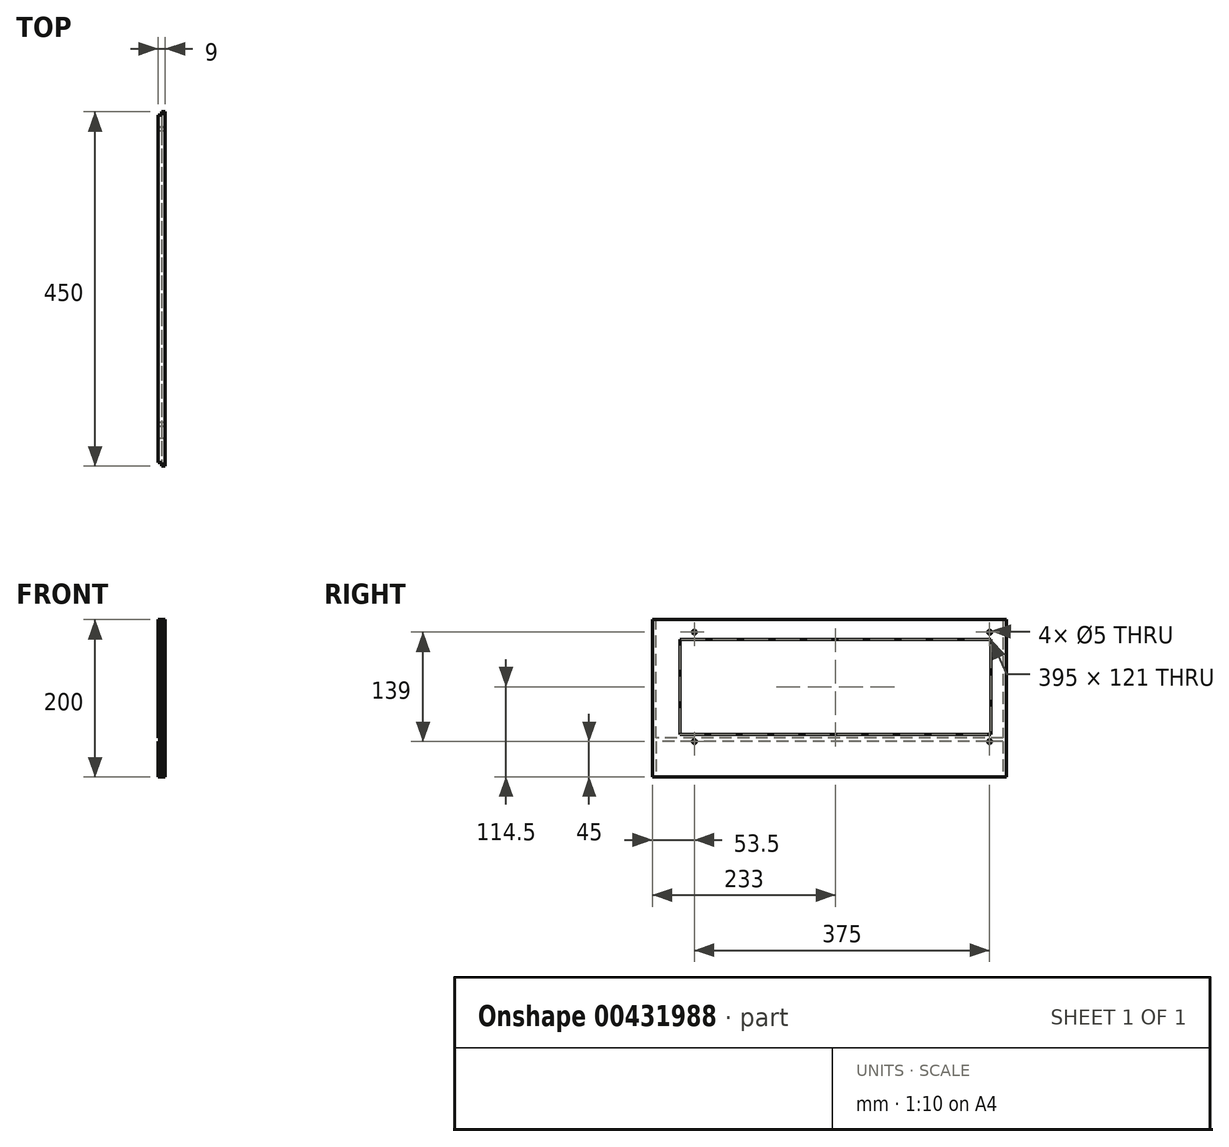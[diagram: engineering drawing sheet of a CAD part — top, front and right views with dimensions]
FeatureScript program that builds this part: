
annotation { "Feature Type Name" : "Feature", "Feature Type Description" : "" }
export const myFeature = defineFeature(function(context is Context, id is Id, definition is map)
    precondition{}
    {
        {
            var Q0;
            Q0=qCreatedBy(makeId("Right.planeOp"),FACE);
            var sketch = newSketch(context, id + "F0", { "sketchPlane" : qUnion([Q0])});
            skLineSegment(sketch, "E0.bottom", {"start": v(-225, 100) * mm, "end": v(225, 100) * mm});
            skLineSegment(sketch, "E0.top", {"start": v(-225, -100) * mm, "end": v(225, -100) * mm});
            skLineSegment(sketch, "E0.left", {"start": v(-225, 100) * mm, "end": v(-225, -100) * mm});
            skLineSegment(sketch, "E0.right", {"start": v(225, 100) * mm, "end": v(225, -100) * mm});
            skPoint(sketch, "E0.middle", {"position": v(0, 0) * mm});
            skSolve(sketch);
        }
        {
            var Q0;
            Q0=makeQuery(id+"F0.imprint","IMPRINT",FACE,{"disambiguationData":[TD([[makeQuery(id+"F0.imprint","IMPRINT",EDGE,{"derivedFrom":sQuery(id+"F0.wireOp",EDGE,"E0.bottom")}),-1.0]])]});
            extrude(context, id + "F1", {"entities" : qUnion([Q0]), "depth" : 9 * mm, "offsetDistance" : 25 * mm});
        }
        {
            var Q0;
            Q0=makeQuery(id+"F1.opExtrude","SWEPT_FACE",FACE,{"disambiguationData":[OSD([sQuery(id+"F0.wireOp",EDGE,"E0.left")])]});
            var sketch = newSketch(context, id + "F2", { "sketchPlane" : qUnion([Q0])});
            skLineSegment(sketch, "E1.bottom", {"start": v(0, -100) * mm, "end": v(4.5, -100) * mm});
            skLineSegment(sketch, "E1.top", {"start": v(0, 100) * mm, "end": v(4.5, 100) * mm});
            skLineSegment(sketch, "E1.left", {"start": v(0, -100) * mm, "end": v(0, 100) * mm});
            skLineSegment(sketch, "E1.right", {"start": v(4.5, -100) * mm, "end": v(4.5, 100) * mm});
            skSolve(sketch);
        }
        {
            var Q0;
            Q0=qSketchRegion(id+"F2",true);
            extrude(context, id + "F3", {"entities" : qUnion([Q0]), "operationType" : NewBodyOperationType.REMOVE, "oppositeDirection" : true, "depth" : 4.5 * mm, "offsetDistance" : 25 * mm});
        }
        {
            var Q0;
            Q0=makeQuery(id+"F1.opExtrude","SWEPT_FACE",FACE,{"disambiguationData":[OSD([sQuery(id+"F0.wireOp",EDGE,"E0.right")])]});
            var sketch = newSketch(context, id + "F4", { "sketchPlane" : qUnion([Q0])});
            skLineSegment(sketch, "E2.bottom", {"start": v(0, 100) * mm, "end": v(-4.5, 100) * mm});
            skLineSegment(sketch, "E2.top", {"start": v(0, -100) * mm, "end": v(-4.5, -100) * mm});
            skLineSegment(sketch, "E2.left", {"start": v(0, 100) * mm, "end": v(0, -100) * mm});
            skLineSegment(sketch, "E2.right", {"start": v(-4.5, 100) * mm, "end": v(-4.5, -100) * mm});
            skSolve(sketch);
        }
        {
            var Q0;
            Q0=qSketchRegion(id+"F4",true);
            extrude(context, id + "F5", {"entities" : qUnion([Q0]), "operationType" : NewBodyOperationType.REMOVE, "oppositeDirection" : true, "depth" : 4.5 * mm, "offsetDistance" : 25 * mm});
        }
        {
            var Q0;
            Q0=makeQuery(id+"F1.opExtrude","CAP_FACE",FACE,{"disambiguationData":[OSD([sQuery(id+"F0.wireOp",EDGE,"E0.bottom"),sQuery(id+"F0.wireOp",EDGE,"E0.top"),sQuery(id+"F0.wireOp",EDGE,"E0.left"),sQuery(id+"F0.wireOp",EDGE,"E0.right")])],"isStart":true});
            var sketch = newSketch(context, id + "F6", { "sketchPlane" : qUnion([Q0])});
            skLineSegment(sketch, "E3.bottom", {"start": v(-220.5, -55) * mm, "end": v(220.5, -55) * mm});
            skLineSegment(sketch, "E3.top", {"start": v(-220.5, -50.5) * mm, "end": v(220.5, -50.5) * mm});
            skLineSegment(sketch, "E3.left", {"start": v(-220.5, -55) * mm, "end": v(-220.5, -50.5) * mm});
            skLineSegment(sketch, "E3.right", {"start": v(220.5, -55) * mm, "end": v(220.5, -50.5) * mm});
            skSolve(sketch);
        }
        {
            var Q0;
            Q0=qSketchRegion(id+"F6",true);
            extrude(context, id + "F7", {"entities" : qUnion([Q0]), "operationType" : NewBodyOperationType.REMOVE, "oppositeDirection" : true, "depth" : 4.5 * mm, "offsetDistance" : 25 * mm});
        }
        {
            var Q0;
            Q0=makeQuery(id+"F1.opExtrude","CAP_FACE",FACE,{"disambiguationData":[OSD([sQuery(id+"F0.wireOp",EDGE,"E0.bottom"),sQuery(id+"F0.wireOp",EDGE,"E0.top"),sQuery(id+"F0.wireOp",EDGE,"E0.left"),sQuery(id+"F0.wireOp",EDGE,"E0.right")])],"isStart":false});
            var sketch = newSketch(context, id + "F8", { "sketchPlane" : qUnion([Q0])});
            skLineSegment(sketch, "E4.bottom", {"start": v(-189.5, 75) * mm, "end": v(205.5, 75) * mm});
            skLineSegment(sketch, "E4.top", {"start": v(-189.5, -46) * mm, "end": v(205.5, -46) * mm});
            skLineSegment(sketch, "E4.left", {"start": v(-189.5, 75) * mm, "end": v(-189.5, -46) * mm});
            skLineSegment(sketch, "E4.right", {"start": v(205.5, 75) * mm, "end": v(205.5, -46) * mm});
            skSolve(sketch);
        }
        {
            var Q0;
            Q0=qSketchRegion(id+"F8",true);
            extrude(context, id + "F9", {"entities" : qUnion([Q0]), "operationType" : NewBodyOperationType.REMOVE, "endBound" : BoundingType.UP_TO_NEXT, "oppositeDirection" : true, "depth" : 25 * mm});
        }
        {
            var Q0;
            Q0=makeQuery(id+"F1.opExtrude","CAP_FACE",FACE,{"disambiguationData":[OSD([sQuery(id+"F0.wireOp",EDGE,"E0.bottom"),sQuery(id+"F0.wireOp",EDGE,"E0.top"),sQuery(id+"F0.wireOp",EDGE,"E0.left"),sQuery(id+"F0.wireOp",EDGE,"E0.right")])],"isStart":false});
            var sketch = newSketch(context, id + "F10", { "sketchPlane" : qUnion([Q0])});
            skCircle(sketch, "E5", {"center": v(203.5, 84) * mm, "radius": 2.5 * mm});
            skCircle(sketch, "E6", {"center": v(-171.5, 84) * mm, "radius": 2.5 * mm});
            skCircle(sketch, "E7", {"center": v(-171.5, -55) * mm, "radius": 2.5 * mm});
            skCircle(sketch, "E8", {"center": v(203.5, -55) * mm, "radius": 2.5 * mm});
            skSolve(sketch);
        }
        {
            var Q0;
            Q0 = qSketchRegion(id + "F10", true);
            extrude(context, id + "F11", {"entities" : qUnion([Q0]), "operationType" : NewBodyOperationType.REMOVE, "endBound" : BoundingType.UP_TO_NEXT, "oppositeDirection" : true, "depth" : 25 * mm});
        }
    });
